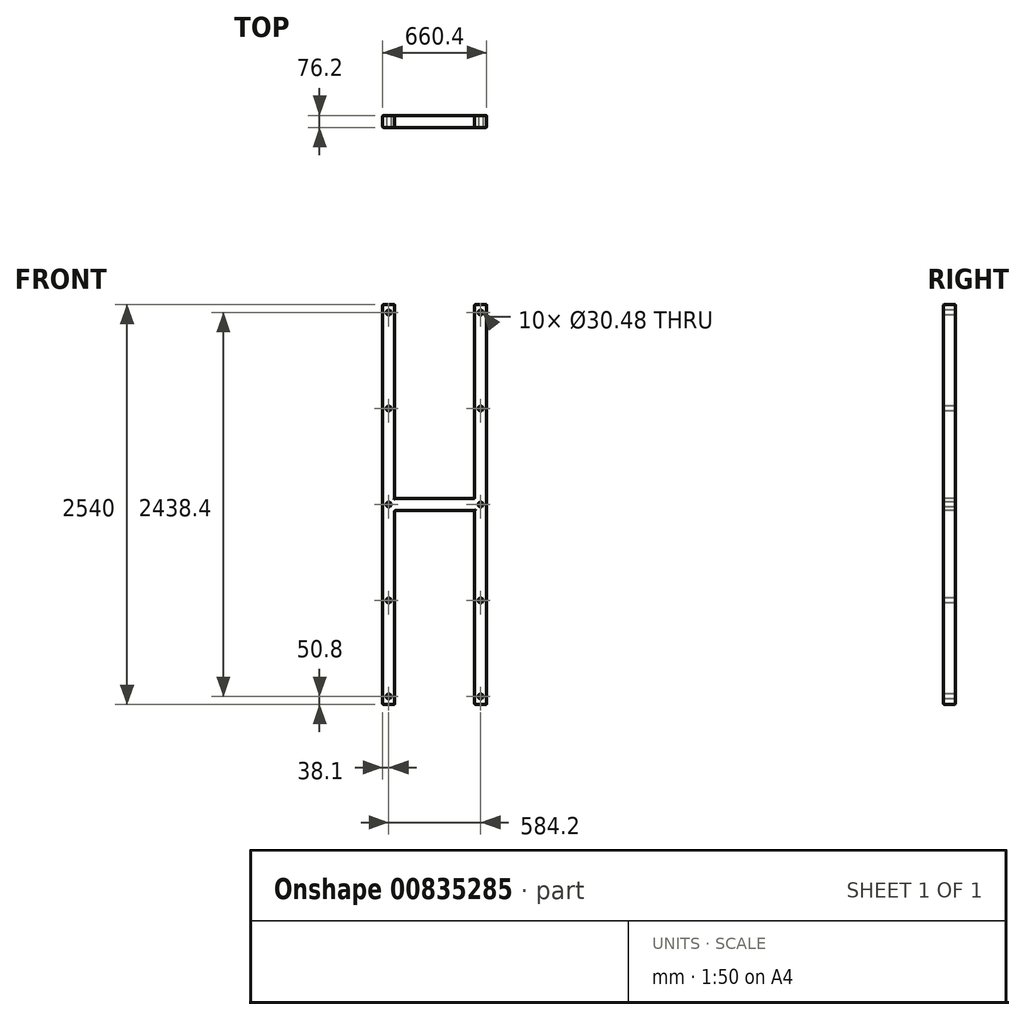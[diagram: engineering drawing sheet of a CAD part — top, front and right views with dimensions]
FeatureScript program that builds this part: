
annotation { "Feature Type Name" : "Feature", "Feature Type Description" : "" }
export const myFeature = defineFeature(function(context is Context, id is Id, definition is map)
    precondition{}
    {
        {
            var Q0;
            Q0=qCreatedBy(makeId("Right.planeOp"),FACE);
            var sketch = newSketch(context, id + "F0", { "sketchPlane" : qUnion([Q0])});
            skLineSegment(sketch, "E0.bottom", {"start": v(38.1, -38.1) * mm, "end": v(-38.1, -38.1) * mm});
            skLineSegment(sketch, "E0.top", {"start": v(38.1, 38.1) * mm, "end": v(-38.1, 38.1) * mm});
            skLineSegment(sketch, "E0.left", {"start": v(38.1, -38.1) * mm, "end": v(38.1, 38.1) * mm});
            skLineSegment(sketch, "E0.right", {"start": v(-38.1, -38.1) * mm, "end": v(-38.1, 38.1) * mm});
            skPoint(sketch, "E0.middle", {"position": v(0, 0) * mm});
            skSolve(sketch);
        }
        {
            var Q0;
            Q0 = qSketchRegion(id + "F0", true);
            extrude(context, id + "F1", {"entities" : qUnion([Q0]), "depth" : 254 * mm, "offsetDistance" : 25.4 * mm, "hasSecondDirection" : true, "secondDirectionOppositeDirection" : true, "secondDirectionDepth" : 254 * mm});
        }
        {
            var Q0;
            Q0=makeQuery(id+"F1.opExtrude","CAP_FACE",FACE,{"disambiguationData":[OSD([sQuery(id+"F0.wireOp",EDGE,"E0.bottom"),sQuery(id+"F0.wireOp",EDGE,"E0.top"),sQuery(id+"F0.wireOp",EDGE,"E0.left"),sQuery(id+"F0.wireOp",EDGE,"E0.right")])],"isStart":false});
            var sketch = newSketch(context, id + "F2", { "sketchPlane" : qUnion([Q0])});
            skLineSegment(sketch, "E1.bottom", {"start": v(38.1, -1270) * mm, "end": v(-38.1, -1270) * mm});
            skLineSegment(sketch, "E1.top", {"start": v(38.1, 1270) * mm, "end": v(-38.1, 1270) * mm});
            skLineSegment(sketch, "E1.left", {"start": v(38.1, -1270) * mm, "end": v(38.1, 1270) * mm});
            skLineSegment(sketch, "E1.right", {"start": v(-38.1, -1270) * mm, "end": v(-38.1, 1270) * mm});
            skPoint(sketch, "E1.middle", {"position": v(0, 0) * mm});
            skSolve(sketch);
        }
        {
            var Q0;
            Q0 = qSketchRegion(id + "F2", true);
            extrude(context, id + "F3", {"entities" : qUnion([Q0]), "operationType" : NewBodyOperationType.ADD, "depth" : 76.2 * mm, "offsetDistance" : 25.4 * mm});
        }
        {
            var Q0;
            Q0=makeQuery(id+"F1.opExtrude","CAP_FACE",FACE,{"disambiguationData":[OSD([sQuery(id+"F0.wireOp",EDGE,"E0.bottom"),sQuery(id+"F0.wireOp",EDGE,"E0.top"),sQuery(id+"F0.wireOp",EDGE,"E0.left"),sQuery(id+"F0.wireOp",EDGE,"E0.right")])],"isStart":true});
            var sketch = newSketch(context, id + "F4", { "sketchPlane" : qUnion([Q0])});
            skLineSegment(sketch, "E2.bottom", {"start": v(38.1, -1270) * mm, "end": v(-38.1, -1270) * mm});
            skLineSegment(sketch, "E2.top", {"start": v(38.1, 1270) * mm, "end": v(-38.1, 1270) * mm});
            skLineSegment(sketch, "E2.left", {"start": v(38.1, -1270) * mm, "end": v(38.1, 1270) * mm});
            skLineSegment(sketch, "E2.right", {"start": v(-38.1, -1270) * mm, "end": v(-38.1, 1270) * mm});
            skPoint(sketch, "E2.middle", {"position": v(0, 0) * mm});
            skSolve(sketch);
        }
        {
            var Q0;
            Q0 = qSketchRegion(id + "F4", true);
            extrude(context, id + "F5", {"entities" : qUnion([Q0]), "operationType" : NewBodyOperationType.ADD, "depth" : 76.2 * mm, "offsetDistance" : 25.4 * mm});
        }
        {
            var Q0;
            Q0=makeQuery(id+"F5.boolean.opBoolean","MERGE",FACE,{"derivedFrom":[makeQuery(id+"F3.boolean.opBoolean","MERGE",FACE,{"derivedFrom":[makeQuery(id+"F1.opExtrude","SWEPT_FACE",FACE,{"disambiguationData":[OSD([sQuery(id+"F0.wireOp",EDGE,"E0.right")])]}),makeQuery(id+"F3.opExtrude","SWEPT_FACE",FACE,{"disambiguationData":[OSD([sQuery(id+"F2.wireOp",EDGE,"E1.right")])]})]}),makeQuery(id+"F5.opExtrude","SWEPT_FACE",FACE,{"disambiguationData":[OSD([sQuery(id+"F4.wireOp",EDGE,"E2.left")])]})]});
            var sketch = newSketch(context, id + "F6", { "sketchPlane" : qUnion([Q0])});
            skCircle(sketch, "E3", {"center": v(-292.1, 1219.2) * mm, "radius": 15.24 * mm});
            skCircle(sketch, "E4.0.1.0", {"center": v(-292.1, 609.6) * mm, "radius": 15.24 * mm});
            skCircle(sketch, "E4.0.2.0", {"center": v(-292.1, 0) * mm, "radius": 15.24 * mm});
            skCircle(sketch, "E4.0.3.0", {"center": v(-292.1, -609.6) * mm, "radius": 15.24 * mm});
            skCircle(sketch, "E4.0.4.0", {"center": v(-292.1, -1219.2) * mm, "radius": 15.24 * mm});
            skLineSegment(sketch, "E4.direction1", {"start": v(-292.1, 1219.2) * mm, "end": v(-266.7, 1219.2) * mm, "construction": true});
            skLineSegment(sketch, "E4.direction2", {"start": v(-292.1, 1219.2) * mm, "end": v(-292.1, 609.6) * mm, "construction": true});
            skLineSegment(sketch, "E5.MirrorCS", {"start": v(292.1, 1219.2) * mm, "end": v(292.1, 609.6) * mm, "construction": true});
            skLineSegment(sketch, "E6.MirrorCS", {"start": v(292.1, 1219.2) * mm, "end": v(266.7, 1219.2) * mm, "construction": true});
            skCircle(sketch, "E7.MirrorC", {"center": v(292.1, 1219.2) * mm, "radius": 15.24 * mm});
            skCircle(sketch, "E8.MirrorC", {"center": v(292.1, 609.6) * mm, "radius": 15.24 * mm});
            skCircle(sketch, "E9.MirrorC", {"center": v(292.1, -1219.2) * mm, "radius": 15.24 * mm});
            skCircle(sketch, "E10.MirrorC", {"center": v(292.1, 0) * mm, "radius": 15.24 * mm});
            skCircle(sketch, "E11.MirrorC", {"center": v(292.1, -609.6) * mm, "radius": 15.24 * mm});
            skSolve(sketch);
        }
        {
            var Q0;
            Q0 = qSketchRegion(id + "F6", true);
            extrude(context, id + "F7", {"entities" : qUnion([Q0]), "operationType" : NewBodyOperationType.REMOVE, "endBound" : BoundingType.THROUGH_ALL, "oppositeDirection" : true, "depth" : 25.4 * mm, "offsetDistance" : 25.4 * mm});
        }
        {
            var Q0;
            Q0=makeQuery(id+"F3.opExtrude","SWEPT_FACE",FACE,{"disambiguationData":[OSD([sQuery(id+"F2.wireOp",EDGE,"E1.top")])]});
            var Q1;
            Q1=makeQuery(id+"F5.opExtrude","SWEPT_FACE",FACE,{"disambiguationData":[OSD([sQuery(id+"F4.wireOp",EDGE,"E2.top")])]});
            fillet(context, id + "F8", {"entities" : qUnion([Q0, Q1]), "radius" : 5.08 * mm, "tangentPropagation" : true, "allowEdgeOverflow" : false});
        }
        {
            var Q0;
            {var subQ0=sQuery(id+"F4.wireOp",EDGE,"E2.left");Q0=makeQuery(id+"F5.boolean.opBoolean","SPLIT",EDGE,{"disambiguationData":[TD([makeQuery(id+"F1.opExtrude","SWEPT_FACE",FACE,{"disambiguationData":[OSD([sQuery(id+"F0.wireOp",EDGE,"E0.top")])]})])],"derivedFrom":makeQuery(id+"F5.opExtrude","CAP_EDGE",EDGE,{"disambiguationData":[OSD([subQ0])],"isStart":true})});}
            var Q1;
            {var subQ0=sQuery(id+"F4.wireOp",EDGE,"E2.right");Q1=makeQuery(id+"F5.boolean.opBoolean","SPLIT",EDGE,{"disambiguationData":[TD([makeQuery(id+"F1.opExtrude","SWEPT_FACE",FACE,{"disambiguationData":[OSD([sQuery(id+"F0.wireOp",EDGE,"E0.top")])]})])],"derivedFrom":makeQuery(id+"F5.opExtrude","CAP_EDGE",EDGE,{"disambiguationData":[OSD([subQ0])],"isStart":true})});}
            var Q2;
            Q2=makeQuery(id+"F1.opExtrude","CAP_EDGE",EDGE,{"disambiguationData":[OSD([sQuery(id+"F0.wireOp",EDGE,"E0.top")])],"isStart":true});
            var Q3;
            Q3=makeQuery(id+"F1.opExtrude","SWEPT_EDGE",EDGE,{"disambiguationData":[OSD([sQuery(id+"F0.wireOp",EDGE,"E0.top"),sQuery(id+"F0.wireOp",EDGE,"E0.left")])]});
            var Q4;
            Q4=makeQuery(id+"F1.opExtrude","SWEPT_EDGE",EDGE,{"disambiguationData":[OSD([sQuery(id+"F0.wireOp",EDGE,"E0.top"),sQuery(id+"F0.wireOp",EDGE,"E0.right")])]});
            var Q5;
            Q5=makeQuery(id+"F1.opExtrude","CAP_EDGE",EDGE,{"disambiguationData":[OSD([sQuery(id+"F0.wireOp",EDGE,"E0.top")])],"isStart":false});
            var Q6;
            {var subQ1=sQuery(id+"F2.wireOp",EDGE,"E1.left");Q6=makeQuery(id+"F3.boolean.opBoolean","SPLIT",EDGE,{"disambiguationData":[TD([makeQuery(id+"F1.opExtrude","SWEPT_FACE",FACE,{"disambiguationData":[OSD([sQuery(id+"F0.wireOp",EDGE,"E0.top")])]})])],"derivedFrom":makeQuery(id+"F3.opExtrude","CAP_EDGE",EDGE,{"disambiguationData":[OSD([subQ1])],"isStart":true})});}
            var Q7;
            {var subQ1=sQuery(id+"F2.wireOp",EDGE,"E1.right");Q7=makeQuery(id+"F3.boolean.opBoolean","SPLIT",EDGE,{"disambiguationData":[TD([makeQuery(id+"F1.opExtrude","SWEPT_FACE",FACE,{"disambiguationData":[OSD([sQuery(id+"F0.wireOp",EDGE,"E0.top")])]})])],"derivedFrom":makeQuery(id+"F3.opExtrude","CAP_EDGE",EDGE,{"disambiguationData":[OSD([subQ1])],"isStart":true})});}
            var Q8;
            Q8=makeQuery(id+"F5.opExtrude","CAP_EDGE",EDGE,{"disambiguationData":[OSD([sQuery(id+"F4.wireOp",EDGE,"E2.left")])],"isStart":false});
            var Q9;
            Q9=makeQuery(id+"F5.opExtrude","CAP_EDGE",EDGE,{"disambiguationData":[OSD([sQuery(id+"F4.wireOp",EDGE,"E2.right")])],"isStart":false});
            var Q10;
            Q10=makeQuery(id+"F1.opExtrude","SWEPT_EDGE",EDGE,{"disambiguationData":[OSD([sQuery(id+"F0.wireOp",EDGE,"E0.bottom"),sQuery(id+"F0.wireOp",EDGE,"E0.right")])]});
            var Q11;
            {var subQ1=sQuery(id+"F2.wireOp",EDGE,"E1.left");Q11=makeQuery(id+"F3.boolean.opBoolean","SPLIT",EDGE,{"disambiguationData":[TD([makeQuery(id+"F1.opExtrude","SWEPT_FACE",FACE,{"disambiguationData":[OSD([sQuery(id+"F0.wireOp",EDGE,"E0.bottom")])]})])],"derivedFrom":makeQuery(id+"F3.opExtrude","CAP_EDGE",EDGE,{"disambiguationData":[OSD([subQ1])],"isStart":true})});}
            var Q12;
            {var subQ0=sQuery(id+"F2.wireOp",EDGE,"E1.right");Q12=makeQuery(id+"F3.boolean.opBoolean","SPLIT",EDGE,{"disambiguationData":[TD([makeQuery(id+"F1.opExtrude","SWEPT_FACE",FACE,{"disambiguationData":[OSD([sQuery(id+"F0.wireOp",EDGE,"E0.bottom")])]})])],"derivedFrom":makeQuery(id+"F3.opExtrude","CAP_EDGE",EDGE,{"disambiguationData":[OSD([subQ0])],"isStart":true})});}
            var Q13;
            {var subQ1=sQuery(id+"F4.wireOp",EDGE,"E2.right");Q13=makeQuery(id+"F5.boolean.opBoolean","SPLIT",EDGE,{"disambiguationData":[TD([makeQuery(id+"F1.opExtrude","SWEPT_FACE",FACE,{"disambiguationData":[OSD([sQuery(id+"F0.wireOp",EDGE,"E0.bottom")])]})])],"derivedFrom":makeQuery(id+"F5.opExtrude","CAP_EDGE",EDGE,{"disambiguationData":[OSD([subQ1])],"isStart":true})});}
            var Q14;
            {var subQ1=sQuery(id+"F4.wireOp",EDGE,"E2.left");Q14=makeQuery(id+"F5.boolean.opBoolean","SPLIT",EDGE,{"disambiguationData":[TD([makeQuery(id+"F1.opExtrude","SWEPT_FACE",FACE,{"disambiguationData":[OSD([sQuery(id+"F0.wireOp",EDGE,"E0.bottom")])]})])],"derivedFrom":makeQuery(id+"F5.opExtrude","CAP_EDGE",EDGE,{"disambiguationData":[OSD([subQ1])],"isStart":true})});}
            var Q15;
            Q15=makeQuery(id+"F3.opExtrude","CAP_EDGE",EDGE,{"disambiguationData":[OSD([sQuery(id+"F2.wireOp",EDGE,"E1.left")])],"isStart":false});
            var Q16;
            Q16=makeQuery(id+"F3.opExtrude","CAP_EDGE",EDGE,{"disambiguationData":[OSD([sQuery(id+"F2.wireOp",EDGE,"E1.right")])],"isStart":false});
            var Q17;
            Q17=makeQuery(id+"F3.opExtrude","SWEPT_FACE",FACE,{"disambiguationData":[OSD([sQuery(id+"F2.wireOp",EDGE,"E1.bottom")])]});
            var Q18;
            Q18=makeQuery(id+"F5.opExtrude","SWEPT_FACE",FACE,{"disambiguationData":[OSD([sQuery(id+"F4.wireOp",EDGE,"E2.bottom")])]});
            var Q19;
            Q19=makeQuery(id+"F1.opExtrude","CAP_EDGE",EDGE,{"disambiguationData":[OSD([sQuery(id+"F0.wireOp",EDGE,"E0.bottom")])],"isStart":true});
            var Q20;
            Q20=makeQuery(id+"F1.opExtrude","CAP_EDGE",EDGE,{"disambiguationData":[OSD([sQuery(id+"F0.wireOp",EDGE,"E0.bottom")])],"isStart":false});
            fillet(context, id + "F9", {"entities" : qUnion([Q0, Q1, Q2, Q3, Q4, Q5, Q6, Q7, Q8, Q9, Q10, Q11, Q12, Q13, Q14, Q15, Q16, Q17, Q18, Q19, Q20]), "radius" : 5.08 * mm, "tangentPropagation" : true, "allowEdgeOverflow" : false});
        }
    });
